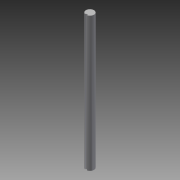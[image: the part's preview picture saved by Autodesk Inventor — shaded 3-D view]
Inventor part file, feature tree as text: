
AUTODESK INVENTOR PART (.ipt)
format: ipt  version: 2014 SP1 (Build 180222100, 222)  size: 76,800 bytes
history: native  units: in
note: dims shown in document units (in); Inventor stores cm internally (conversion verified against a paired STEP export)
features: extrude x1, sketch x1
ambient origin geometry x8: Origin, YZ Plane, XZ Plane, XY Plane, X Axis, Y Axis, Z Axis, Center Point
bodies: Solid1 (feature_tree)
feature tree (2):
  extrude  "Extrusion1"  Depth=0.0787in
  sketch  "Sketch1"  dims[d0=0.315in d1=0.0787in d2=0.0394in d3=0.0394in d4=5.25in d5=0.0in]
